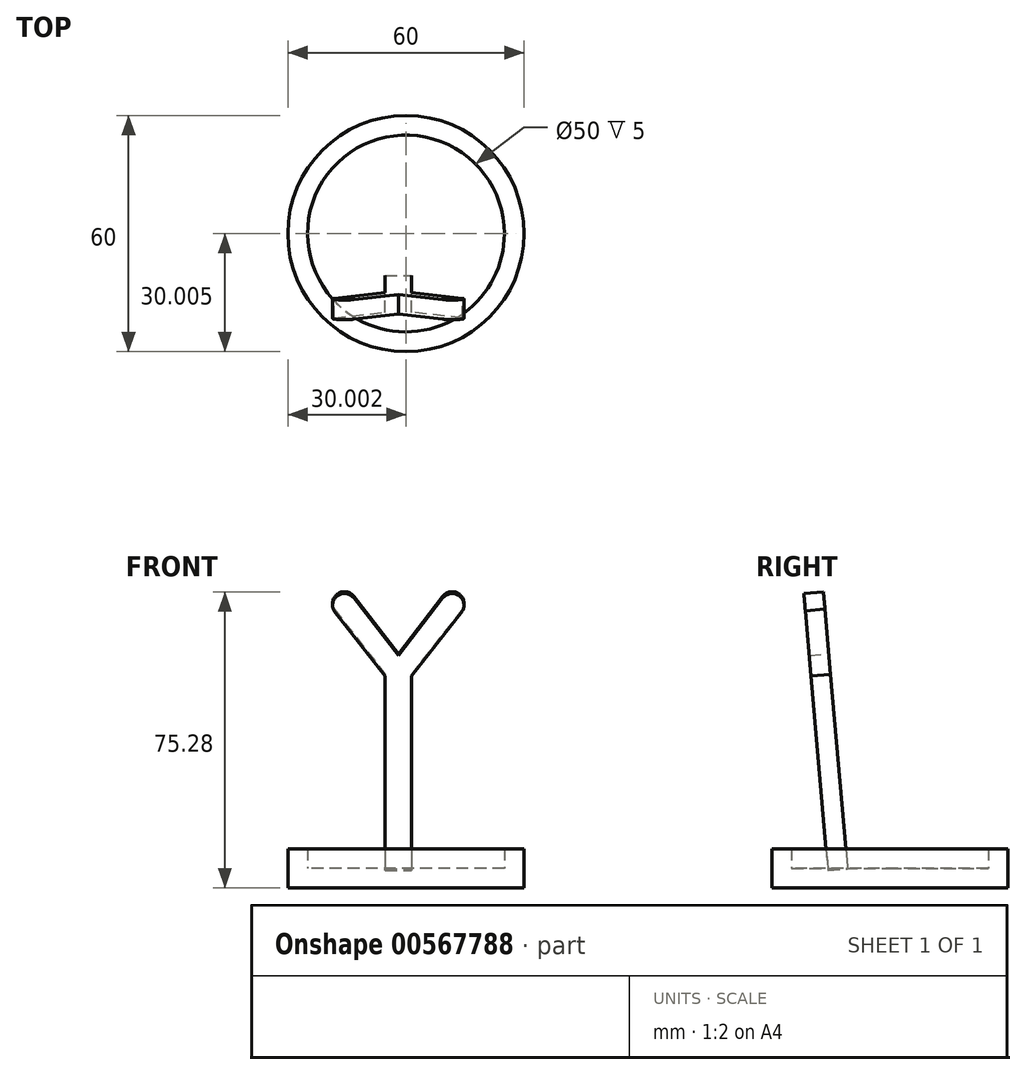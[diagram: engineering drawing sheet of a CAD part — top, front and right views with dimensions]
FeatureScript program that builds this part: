
annotation { "Feature Type Name" : "Feature", "Feature Type Description" : "" }
export const myFeature = defineFeature(function(context is Context, id is Id, definition is map)
    precondition{}
    {
        {
            var Q0;
            Q0=qCreatedBy(makeId("Front.planeOp"),FACE);
            var sketch = newSketch(context, id + "F0", { "sketchPlane" : qUnion([Q0])});
            skLineSegment(sketch, "E0.bottom", {"start": v(-23.85, 27.85) * mm, "end": v(0, 27.85) * mm, "construction": true});
            skLineSegment(sketch, "E0.top", {"start": v(-23.85, -54.8) * mm, "end": v(0, -54.8) * mm, "construction": true});
            skLineSegment(sketch, "E0.left", {"start": v(-23.85, 27.85) * mm, "end": v(-23.85, -54.8) * mm, "construction": true});
            skLineSegment(sketch, "E0.right", {"start": v(0, 27.85) * mm, "end": v(0, -54.8) * mm, "construction": true});
            skLineSegment(sketch, "E1", {"start": v(0, 0) * mm, "end": v(-11.28, 14.67) * mm});
            skArc(sketch, "E2", {"start": v(-11.28, 14.67) * mm, "mid": v(-15.3, 15.37) * mm, "end": v(-16.33, 11.41) * mm});
            skLineSegment(sketch, "E3", {"start": v(-16.33, 11.41) * mm, "end": v(-3.33, -5.22) * mm});
            skLineSegment(sketch, "E4", {"start": v(-3.33, -5.22) * mm, "end": v(-3.33, -54.8) * mm});
            skLineSegment(sketch, "E5", {"start": v(-3.33, -54.8) * mm, "end": v(0, -54.8) * mm});
            skLineSegment(sketch, "E6", {"start": v(0, -54.8) * mm, "end": v(0, 0) * mm});
            skArc(sketch, "E7.MirrorCS", {"start": v(11.28, 14.67) * mm, "mid": v(15.3, 15.37) * mm, "end": v(16.33, 11.41) * mm});
            skLineSegment(sketch, "E8.MirrorCS", {"start": v(0, 0) * mm, "end": v(11.28, 14.67) * mm});
            skLineSegment(sketch, "E9.MirrorCS", {"start": v(16.33, 11.41) * mm, "end": v(3.33, -5.22) * mm});
            skLineSegment(sketch, "E10.MirrorCS", {"start": v(3.33, -5.22) * mm, "end": v(3.33, -54.8) * mm});
            skLineSegment(sketch, "E11.MirrorCS", {"start": v(3.33, -54.8) * mm, "end": v(0, -54.8) * mm});
            skSolve(sketch);
        }
        {
            var Q0;
            Q0=makeQuery(id+"F0.imprint","IMPRINT",FACE,{"disambiguationData":[TD([[makeQuery(id+"F0.imprint","IMPRINT",EDGE,{"derivedFrom":sQuery(id+"F0.wireOp",EDGE,"E1")}),1.0]])]});
            var Q1;
            Q1=makeQuery(id+"F0.imprint","IMPRINT",FACE,{"disambiguationData":[TD([[makeQuery(id+"F0.imprint","IMPRINT",EDGE,{"derivedFrom":sQuery(id+"F0.wireOp",EDGE,"E6")}),-1.0]])]});
            extrude(context, id + "F1", {"entities" : qUnion([Q0, Q1]), "depth" : 5 * mm, "offsetDistance" : 25 * mm});
        }
        {
            var Q0;
            Q0=makeQuery(id+"F1.opExtrude","SWEPT_BODY",BODY,{"disambiguationData":[OSD([sQuery(id+"F0.wireOp",EDGE,"E1"),sQuery(id+"F0.wireOp",EDGE,"E2"),sQuery(id+"F0.wireOp",EDGE,"E3"),sQuery(id+"F0.wireOp",EDGE,"E4"),sQuery(id+"F0.wireOp",EDGE,"E5"),sQuery(id+"F0.wireOp",EDGE,"E7.MirrorCS"),sQuery(id+"F0.wireOp",EDGE,"E8.MirrorCS"),sQuery(id+"F0.wireOp",EDGE,"E9.MirrorCS"),sQuery(id+"F0.wireOp",EDGE,"E10.MirrorCS"),sQuery(id+"F0.wireOp",EDGE,"E11.MirrorCS")])]});
            var Q1;
            Q1=makeQuery(id+"F1.opExtrude","CAP_EDGE",EDGE,{"disambiguationData":[OSD([sQuery(id+"F0.wireOp",EDGE,"E5"),sQuery(id+"F0.wireOp",EDGE,"E11.MirrorCS")])],"isStart":true});
            transform(context, id + "F2", {"entities" : qUnion([Q0]), "transformType" : TransformType.ROTATION, "transformAxis" : qUnion([Q1]), "angle" : 90 * degree, "oppositeDirection" : true, "makeCopy" : false});
        }
        {
            var Q0;
            Q0=qCreatedBy(makeId("Top.planeOp"),FACE);
            var sketch = newSketch(context, id + "F3", { "sketchPlane" : qUnion([Q0])});
            skCircle(sketch, "E12", {"center": v(-27.25, -7.69) * mm, "radius": 30 * mm});
            skSolve(sketch);
        }
        {
            var Q0;
            Q0=makeQuery(id+"F3.imprint","IMPRINT",FACE,{"disambiguationData":[TD([[makeQuery(id+"F3.imprint","IMPRINT",EDGE,{"derivedFrom":sQuery(id+"F3.wireOp",EDGE,"E12")}),1.0]])]});
            extrude(context, id + "F4", {"entities" : qUnion([Q0]), "depth" : 10 * mm, "offsetDistance" : 25 * mm});
        }
        {
            var Q0;
            Q0=makeQuery(id+"F4.opExtrude","CAP_FACE",FACE,{"disambiguationData":[OSD([sQuery(id+"F3.wireOp",EDGE,"E12")])],"isStart":false});
            shell(context, id + "F5", {"entities" : qUnion([Q0]), "thickness" : 5 * mm});
        }
        {
            var Q0;
            Q0=makeQuery(id+"F1.opExtrude","SWEPT_BODY",BODY,{"disambiguationData":[OSD([sQuery(id+"F0.wireOp",EDGE,"E1"),sQuery(id+"F0.wireOp",EDGE,"E2"),sQuery(id+"F0.wireOp",EDGE,"E3"),sQuery(id+"F0.wireOp",EDGE,"E4"),sQuery(id+"F0.wireOp",EDGE,"E5"),sQuery(id+"F0.wireOp",EDGE,"E7.MirrorCS"),sQuery(id+"F0.wireOp",EDGE,"E8.MirrorCS"),sQuery(id+"F0.wireOp",EDGE,"E9.MirrorCS"),sQuery(id+"F0.wireOp",EDGE,"E10.MirrorCS"),sQuery(id+"F0.wireOp",EDGE,"E11.MirrorCS")])]});
            transform(context, id + "F6", {"entities" : qUnion([Q0]), "transformType" : TransformType.TRANSLATION_3D, "dx" : -10.5 * mm, "dy" : -18.4 * mm, "dz" : 60.1 * mm, "makeCopy" : false});
        }
        {
            var Q0;
            Q0=makeQuery(id+"F1.opExtrude","SWEPT_BODY",BODY,{"disambiguationData":[OSD([sQuery(id+"F0.wireOp",EDGE,"E1"),sQuery(id+"F0.wireOp",EDGE,"E2"),sQuery(id+"F0.wireOp",EDGE,"E3"),sQuery(id+"F0.wireOp",EDGE,"E4"),sQuery(id+"F0.wireOp",EDGE,"E5"),sQuery(id+"F0.wireOp",EDGE,"E7.MirrorCS"),sQuery(id+"F0.wireOp",EDGE,"E8.MirrorCS"),sQuery(id+"F0.wireOp",EDGE,"E9.MirrorCS"),sQuery(id+"F0.wireOp",EDGE,"E10.MirrorCS"),sQuery(id+"F0.wireOp",EDGE,"E11.MirrorCS")])]});
            var Q1;
            Q1=makeQuery(id+"F1.opExtrude","CAP_EDGE",EDGE,{"disambiguationData":[OSD([sQuery(id+"F0.wireOp",EDGE,"E5"),sQuery(id+"F0.wireOp",EDGE,"E11.MirrorCS")])],"isStart":true});
            transform(context, id + "F7", {"entities" : qUnion([Q0]), "transformType" : TransformType.ROTATION, "transformAxis" : qUnion([Q1]), "angle" : 95 * degree, "makeCopy" : false});
        }
        {
            var Q0;
            Q0=makeQuery(id+"F1.opExtrude","SWEPT_BODY",BODY,{"disambiguationData":[OSD([sQuery(id+"F0.wireOp",EDGE,"E1"),sQuery(id+"F0.wireOp",EDGE,"E2"),sQuery(id+"F0.wireOp",EDGE,"E3"),sQuery(id+"F0.wireOp",EDGE,"E4"),sQuery(id+"F0.wireOp",EDGE,"E5"),sQuery(id+"F0.wireOp",EDGE,"E7.MirrorCS"),sQuery(id+"F0.wireOp",EDGE,"E8.MirrorCS"),sQuery(id+"F0.wireOp",EDGE,"E9.MirrorCS"),sQuery(id+"F0.wireOp",EDGE,"E10.MirrorCS"),sQuery(id+"F0.wireOp",EDGE,"E11.MirrorCS")])]});
            transform(context, id + "F8", {"entities" : qUnion([Q0]), "transformType" : TransformType.TRANSLATION_3D, "dx" : -18.7 * mm, "dy" : 0 * mm, "dz" : -0.4 * mm, "makeCopy" : false});
        }
    });
